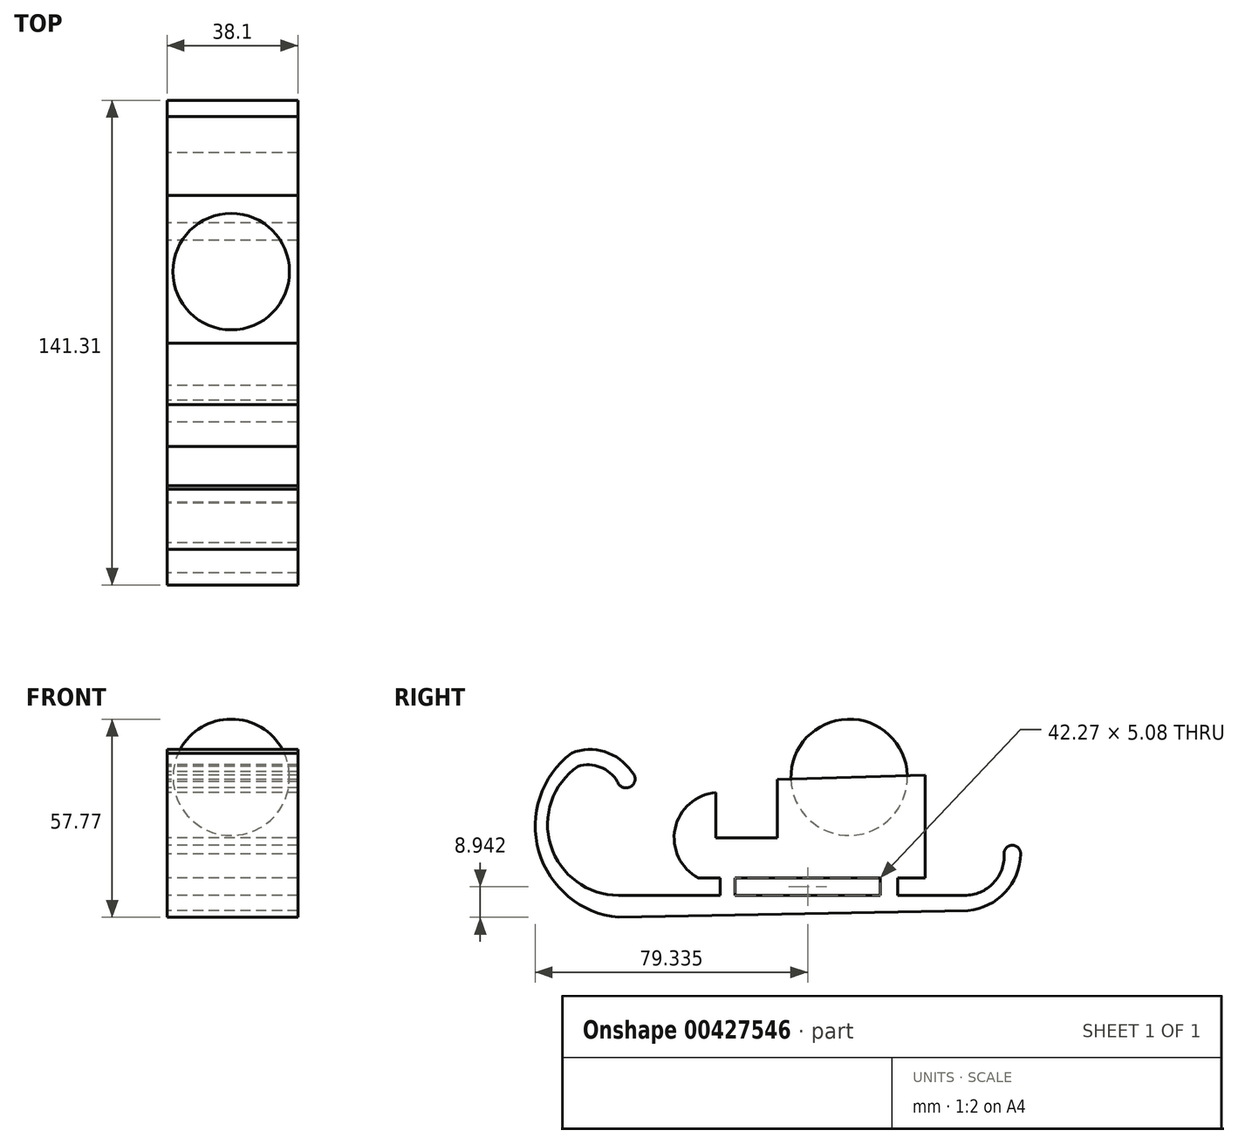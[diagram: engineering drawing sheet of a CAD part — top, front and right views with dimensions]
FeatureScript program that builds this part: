
annotation { "Feature Type Name" : "Feature", "Feature Type Description" : "" }
export const myFeature = defineFeature(function(context is Context, id is Id, definition is map)
    precondition{}
    {
        {
            var Q0;
            Q0=qCreatedBy(makeId("Right.planeOp"),FACE);
            var sketch = newSketch(context, id + "F0", { "sketchPlane" : qUnion([Q0])});
            skLineSegment(sketch, "E0", {"start": v(55.35, 12.92) * mm, "end": v(55.35, -17.07) * mm});
            skLineSegment(sketch, "E1", {"start": v(55.35, -17.07) * mm, "end": v(0, -17.07) * mm});
            skArc(sketch, "E2", {"start": v(-5.58, 7.82) * mm, "mid": v(-17.5, -2.7) * mm, "end": v(-10.69, -17.07) * mm});
            skLineSegment(sketch, "E3", {"start": v(-5.58, 7.82) * mm, "end": v(-5.58, -5.36) * mm});
            skLineSegment(sketch, "E4", {"start": v(-5.58, -5.36) * mm, "end": v(12.28, -5.36) * mm});
            skLineSegment(sketch, "E5", {"start": v(12.28, -5.36) * mm, "end": v(12.28, 11.64) * mm});
            skLineSegment(sketch, "E6", {"start": v(12.28, 11.64) * mm, "end": v(55.35, 12.92) * mm});
            skLineSegment(sketch, "E7", {"start": v(47.35, -17.07) * mm, "end": v(47.35, -22.15) * mm});
            skLineSegment(sketch, "E8", {"start": v(42.27, -17.07) * mm, "end": v(42.27, -22.15) * mm});
            skLineSegment(sketch, "E9", {"start": v(42.27, -22.15) * mm, "end": v(0, -22.15) * mm});
            skArc(sketch, "E10", {"start": v(-45.78, 15.47) * mm, "mid": v(-53.69, -7.67) * mm, "end": v(-33.98, -22.15) * mm});
            skArc(sketch, "E11", {"start": v(-34.3, 11) * mm, "mid": v(-39.26, 15.23) * mm, "end": v(-45.78, 15.47) * mm});
            skArc(sketch, "E12", {"start": v(-34.3, 11) * mm, "mid": v(-30.28, 9.64) * mm, "end": v(-30.15, 13.88) * mm});
            skArc(sketch, "E13", {"start": v(-30.15, 13.88) * mm, "mid": v(-37.96, 19.7) * mm, "end": v(-47.7, 19.3) * mm});
            skLineSegment(sketch, "E14", {"start": v(47.35, -22.15) * mm, "end": v(66.83, -22.15) * mm});
            skArc(sketch, "E15", {"start": v(66.83, -22.15) * mm, "mid": v(75.17, -18.56) * mm, "end": v(78.32, -10.05) * mm});
            skArc(sketch, "E16", {"start": v(83.1, -10.05) * mm, "mid": v(80.71, -7.54) * mm, "end": v(78.32, -10.05) * mm});
            skArc(sketch, "E17", {"start": v(67.8, -26.64) * mm, "mid": v(78.58, -21.23) * mm, "end": v(83.1, -10.05) * mm});
            skArc(sketch, "E18", {"start": v(-47.7, 19.3) * mm, "mid": v(-57.17, -9.3) * mm, "end": v(-33.98, -28.55) * mm});
            skLineSegment(sketch, "E19", {"start": v(-33.98, -28.55) * mm, "end": v(67.8, -26.64) * mm});
            skLineSegment(sketch, "E20", {"start": v(0, -17.07) * mm, "end": v(0, -22.15) * mm});
            skLineSegment(sketch, "E21", {"start": v(-4.34, -17.07) * mm, "end": v(-4.34, -22.15) * mm});
            skLineSegment(sketch, "E22.trimOffspring", {"start": v(-4.34, -22.15) * mm, "end": v(-33.98, -22.15) * mm});
            skLineSegment(sketch, "E23.trimOffspring", {"start": v(-4.34, -17.07) * mm, "end": v(-10.69, -17.07) * mm});
            skSolve(sketch);
        }
        {
            var Q0;
            Q0 = qSketchRegion(id + "F0", true);
            extrude(context, id + "F1", {"entities" : qUnion([Q0]), "depth" : 38.1 * mm});
        }
        {
            var Q0;
            Q0=makeQuery(id+"F1.opExtrude","SWEPT_FACE",FACE,{"disambiguationData":[OSD([sQuery(id+"F0.wireOp",EDGE,"E6")])]});
            var sketch = newSketch(context, id + "F2", { "sketchPlane" : qUnion([Q0])});
            skArc(sketch, "E24", {"start": v(18.67, 16.58) * mm, "mid": v(35.63, 33.53) * mm, "end": v(18.67, 50.49) * mm});
            skLineSegment(sketch, "E25", {"start": v(18.67, 50.49) * mm, "end": v(18.67, 16.58) * mm});
            skSolve(sketch);
        }
        {
            var Q0;
            Q0=makeQuery(id+"F2.imprint","IMPRINT",FACE,{"disambiguationData":[TD([[makeQuery(id+"F2.imprint","IMPRINT",EDGE,{"derivedFrom":sQuery(id+"F2.wireOp",EDGE,"E24")}),1.0]])]});
            var Q1;
            Q1=sQuery(id+"F2.wireOp",EDGE,"E25");
            revolve(context, id + "F3", {"entities" : qUnion([Q0]), "axis" : qUnion([Q1]), "revolveType" : RevolveType.FULL});
        }
    });
